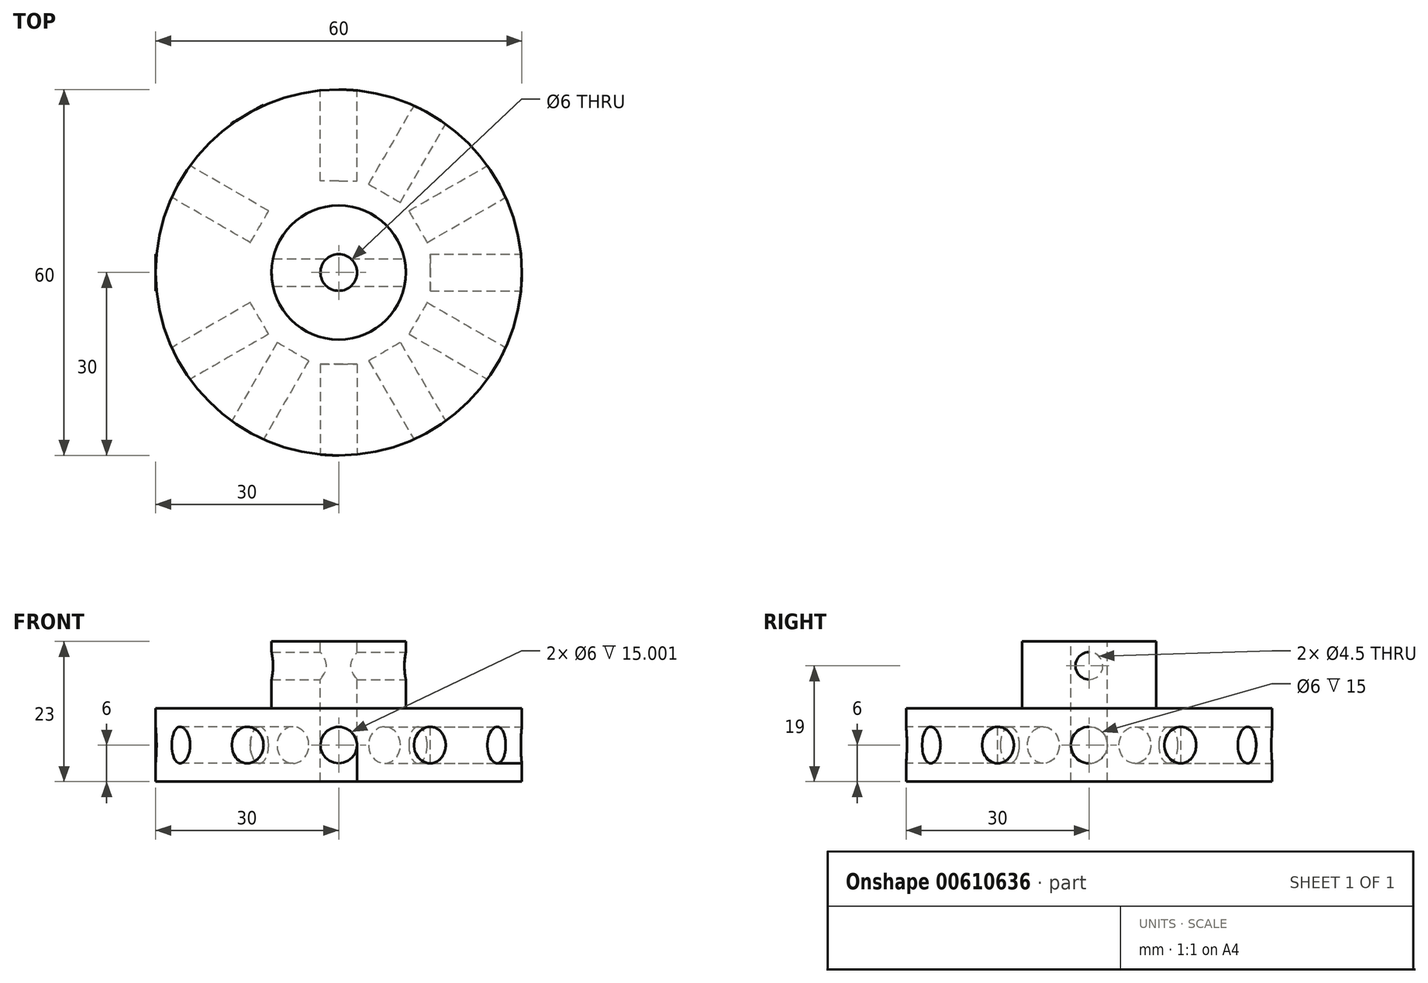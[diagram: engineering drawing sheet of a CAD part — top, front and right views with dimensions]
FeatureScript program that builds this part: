
annotation { "Feature Type Name" : "Feature", "Feature Type Description" : "" }
export const myFeature = defineFeature(function(context is Context, id is Id, definition is map)
    precondition{}
    {
        {
            assignVariable(context, id + "F0", {"name" : "Diam", "anyValue" : 60});
        }
        {
            assignVariable(context, id + "F1", {"name" : "Shaft_Dia", "anyValue" : 6});
        }
        {
            assignVariable(context, id + "F2", {"name" : "Hole_Depth", "anyValue" : 15});
        }
        {
            assignVariable(context, id + "F3", {"name" : "Hub_Thickness", "anyValue" : 12});
        }
        {
            var Q0;
            Q0=qCreatedBy(makeId("Top.planeOp"),FACE);
            var sketch = newSketch(context, id + "F4", { "sketchPlane" : qUnion([Q0])});
            skCircle(sketch, "E0", {"center": v(0, 0) * mm, "radius": 30 * mm});
            skSolve(sketch);
        }
        {
            var Q0;
            Q0=makeQuery(id+"F4.imprint","IMPRINT",FACE,{"disambiguationData":[TD([[makeQuery(id+"F4.imprint","IMPRINT",EDGE,{"derivedFrom":sQuery(id+"F4.wireOp",EDGE,"E0")}),1.0]])]});
            extrude(context, id + "F5", {"entities" : qUnion([Q0]), "depth" : (getVariable(context, 'Hub_Thickness')) * mm, "offsetDistance" : 25 * mm});
        }
        {
            var Q0;
            Q0=makeQuery(id+"F5.opExtrude","CAP_FACE",FACE,{"disambiguationData":[OSD([sQuery(id+"F4.wireOp",EDGE,"E0")])],"isStart":false});
            var sketch = newSketch(context, id + "F6", { "sketchPlane" : qUnion([Q0])});
            skCircle(sketch, "E1", {"center": v(0, 0) * mm, "radius": 11 * mm});
            skSolve(sketch);
        }
        {
            var Q0;
            Q0=makeQuery(id+"F6.imprint","IMPRINT",FACE,{"disambiguationData":[TD([[makeQuery(id+"F6.imprint","IMPRINT",EDGE,{"derivedFrom":sQuery(id+"F6.wireOp",EDGE,"E1")}),1.0]])]});
            extrude(context, id + "F7", {"entities" : qUnion([Q0]), "operationType" : NewBodyOperationType.ADD, "depth" : 11 * mm, "offsetDistance" : 25 * mm});
        }
        {
            var Q0;
            Q0=makeQuery(id+"F7.opExtrude","CAP_FACE",FACE,{"disambiguationData":[OSD([sQuery(id+"F6.wireOp",EDGE,"E1")])],"isStart":false});
            var sketch = newSketch(context, id + "F8", { "sketchPlane" : qUnion([Q0])});
            skPoint(sketch, "E2", {"position": v(0, 0) * mm});
            skSolve(sketch);
        }
        {
            var Q0;
            Q0=sQuery(id+"F8.wireOp",VERTEX,"E2");
            var Q1;
            Q1=makeQuery(id+"F5.opExtrude","SWEPT_BODY",BODY,{"disambiguationData":[OSD([sQuery(id+"F4.wireOp",EDGE,"E0")])]});
            hole(context, id + "F9", {"style" : HoleStyle.SIMPLE, "endStyle" : HoleEndStyle.THROUGH, "holeDiameter" : (getVariable(context, 'Shaft_Dia')) * mm, "majorDiameter" : 5 * mm, "tappedDepth" : 12 * mm, "tapClearance" : 3, "locations" : qUnion([Q0]), "scope" : qUnion([Q1])});
        }
        {
            var Q0;
            Q0=qCreatedBy(makeId("Right.planeOp"),FACE);
            var sketch = newSketch(context, id + "F10", { "sketchPlane" : qUnion([Q0])});
            skCircle(sketch, "E3", {"center": v(0, 19) * mm, "radius": 2.25 * mm});
            skSolve(sketch);
        }
        {
            var Q0;
            Q0 = qSketchRegion(id + "F10", true);
            extrude(context, id + "F11", {"entities" : qUnion([Q0]), "operationType" : NewBodyOperationType.REMOVE, "endBound" : BoundingType.SYMMETRIC, "oppositeDirection" : true, "depth" : 100 * mm, "offsetDistance" : 25 * mm});
        }
        {
            var Q0;
            Q0=qCreatedBy(makeId("Top.planeOp"),FACE);
            var sketch = newSketch(context, id + "F12", { "sketchPlane" : qUnion([Q0])});
            skPoint(sketch, "E4", {"position": v(-30, 0) * mm});
            skPoint(sketch, "E5.1.0", {"position": v(-25.98, -15) * mm});
            skPoint(sketch, "E5.2.0", {"position": v(-15, -25.98) * mm});
            skPoint(sketch, "E5.3.0", {"position": v(0, -30) * mm});
            skPoint(sketch, "E5.4.0", {"position": v(15, -25.98) * mm});
            skPoint(sketch, "E5.5.0", {"position": v(25.98, -15) * mm});
            skPoint(sketch, "E5.6.0", {"position": v(30, 0) * mm});
            skPoint(sketch, "E5.7.0", {"position": v(25.98, 15) * mm});
            skPoint(sketch, "E5.8.0", {"position": v(15, 25.98) * mm});
            skPoint(sketch, "E5.9.0", {"position": v(0, 30) * mm});
            skPoint(sketch, "E5.10.0", {"position": v(-15, 25.98) * mm});
            skPoint(sketch, "E5.11.0", {"position": v(-25.98, 15) * mm});
            skPoint(sketch, "E5.center", {"position": v(0, 0) * mm});
            skSolve(sketch);
        }
        {
            var Q0;
            Q0=qCreatedBy(makeId("Front.planeOp"),FACE);
            cPlane(context, id + "F13", {"entities" : qUnion([Q0]), "cplaneType" : CPlaneType.OFFSET, "offset" : (getVariable(context, 'Diam') / 2) * mm, "width" : 150 * mm, "height" : 150 * mm});
        }
        {
            var Q0;
            Q0=qCreatedBy(id+"F13.planeOp",FACE);
            var sketch = newSketch(context, id + "F14", { "sketchPlane" : qUnion([Q0])});
            skCircle(sketch, "E6", {"center": v(0, 6) * mm, "radius": 3 * mm});
            skSolve(sketch);
        }
        {
            var Q0;
            Q0=makeQuery(id+"F14.imprint","IMPRINT",FACE,{"disambiguationData":[TD([[makeQuery(id+"F14.imprint","IMPRINT",EDGE,{"derivedFrom":sQuery(id+"F14.wireOp",EDGE,"E6")}),1.0]])]});
            var Q1;
            Q1=sQuery(id+"F14.wireOp",EDGE,"E6");
            extrude(context, id + "F15", {"entities" : qUnion([Q0]), "operationType" : NewBodyOperationType.REMOVE, "surfaceEntities" : qUnion([Q1]), "oppositeDirection" : true, "depth" : (getVariable(context, 'Hole_Depth')) * mm, "offsetDistance" : 25 * mm});
        }
        {
            var Q0;
            Q0=qCreatedBy(makeId("Front.planeOp"),FACE);
            cPlane(context, id + "F16", {"entities" : qUnion([Q0]), "cplaneType" : CPlaneType.OFFSET, "offset" : (getVariable(context, 'Diam') / 2) * mm, "oppositeDirection" : true, "width" : 150 * mm, "height" : 150 * mm});
        }
        {
            var Q0;
            Q0=qCreatedBy(id+"F16.planeOp",FACE);
            var sketch = newSketch(context, id + "F17", { "sketchPlane" : qUnion([Q0])});
            skCircle(sketch, "E7", {"center": v(0, 6) * mm, "radius": 3 * mm});
            skSolve(sketch);
        }
        {
            var Q0;
            Q0=makeQuery(id+"F17.imprint","IMPRINT",FACE,{"disambiguationData":[TD([[makeQuery(id+"F17.imprint","IMPRINT",EDGE,{"derivedFrom":sQuery(id+"F17.wireOp",EDGE,"E7")}),1.0]])]});
            var Q1;
            Q1=sQuery(id+"F17.wireOp",EDGE,"E7");
            extrude(context, id + "F18", {"entities" : qUnion([Q0]), "operationType" : NewBodyOperationType.REMOVE, "surfaceEntities" : qUnion([Q1]), "depth" : (getVariable(context, 'Hole_Depth')) * mm, "offsetDistance" : 25 * mm});
        }
        {
            var Q0;
            Q0=qCreatedBy(makeId("Right.planeOp"),FACE);
            cPlane(context, id + "F19", {"entities" : qUnion([Q0]), "cplaneType" : CPlaneType.OFFSET, "offset" : (getVariable(context, 'Diam') / 2) * mm, "width" : 150 * mm, "height" : 150 * mm});
        }
        {
            var Q0;
            Q0=qCreatedBy(id+"F19.planeOp",FACE);
            var sketch = newSketch(context, id + "F20", { "sketchPlane" : qUnion([Q0])});
            skCircle(sketch, "E8", {"center": v(0, 6) * mm, "radius": 3 * mm});
            skSolve(sketch);
        }
        {
            var Q0;
            Q0=makeQuery(id+"F20.imprint","IMPRINT",FACE,{"disambiguationData":[TD([[makeQuery(id+"F20.imprint","IMPRINT",EDGE,{"derivedFrom":sQuery(id+"F20.wireOp",EDGE,"E8")}),1.0]])]});
            extrude(context, id + "F21", {"entities" : qUnion([Q0]), "operationType" : NewBodyOperationType.REMOVE, "oppositeDirection" : true, "depth" : (getVariable(context, 'Hole_Depth')) * mm, "offsetDistance" : 25 * mm});
        }
        {
            var Q0;
            Q0=qCreatedBy(makeId("Right.planeOp"),FACE);
            cPlane(context, id + "F22", {"entities" : qUnion([Q0]), "cplaneType" : CPlaneType.OFFSET, "offset" : (getVariable(context, 'Diam') / 2) * mm, "oppositeDirection" : true, "width" : 150 * mm, "height" : 150 * mm});
        }
        {
            var Q0;
            Q0=qCreatedBy(id+"F22.planeOp",FACE);
            var sketch = newSketch(context, id + "F23", { "sketchPlane" : qUnion([Q0])});
            skCircle(sketch, "E9", {"center": v(0, 6) * mm, "radius": 3 * mm});
            skSolve(sketch);
        }
        {
            var Q0;
            Q0=makeQuery(id+"F23.imprint","IMPRINT",FACE,{"disambiguationData":[TD([[makeQuery(id+"F23.imprint","IMPRINT",EDGE,{"derivedFrom":sQuery(id+"F23.wireOp",EDGE,"E9")}),1.0]])]});
            var Q1;
            Q1=sQuery(id+"F23.wireOp",EDGE,"E9");
            extrude(context, id + "F24", {"entities" : qUnion([Q0]), "operationType" : NewBodyOperationType.ADD, "surfaceEntities" : qUnion([Q1]), "depth" : (getVariable(context, 'Hole_Depth')) * mm, "offsetDistance" : 25 * mm});
        }
        {
            var Q0;
            Q0=sQuery(id+"F12.wireOp",VERTEX,"E5.11.0");
            var Q1;
            Q1=makeQuery(id+"F5.opExtrude","CAP_EDGE",EDGE,{"disambiguationData":[OSD([sQuery(id+"F4.wireOp",EDGE,"E0")])],"isStart":false});
            cPlane(context, id + "F25", {"entities" : qUnion([Q0, Q1]), "cplaneType" : CPlaneType.CURVE_POINT, "offset" : 25 * mm, "width" : 150 * mm, "height" : 150 * mm});
        }
        {
            var Q0;
            Q0=sQuery(id+"F12.wireOp",VERTEX,"E5.10.0");
            var Q1;
            Q1=makeQuery(id+"F5.opExtrude","CAP_EDGE",EDGE,{"disambiguationData":[OSD([sQuery(id+"F4.wireOp",EDGE,"E0")])],"isStart":false});
            cPlane(context, id + "F26", {"entities" : qUnion([Q0, Q1]), "cplaneType" : CPlaneType.CURVE_POINT, "offset" : 25 * mm, "width" : 150 * mm, "height" : 150 * mm});
        }
        {
            var Q0;
            Q0=sQuery(id+"F12.wireOp",VERTEX,"E5.8.0");
            var Q1;
            Q1=makeQuery(id+"F5.opExtrude","CAP_EDGE",EDGE,{"disambiguationData":[OSD([sQuery(id+"F4.wireOp",EDGE,"E0")])],"isStart":false});
            cPlane(context, id + "F27", {"entities" : qUnion([Q0, Q1]), "cplaneType" : CPlaneType.CURVE_POINT, "offset" : 25 * mm, "width" : 150 * mm, "height" : 150 * mm});
        }
        {
            var Q0;
            Q0=sQuery(id+"F12.wireOp",VERTEX,"E5.7.0");
            var Q1;
            Q1=makeQuery(id+"F5.opExtrude","CAP_EDGE",EDGE,{"disambiguationData":[OSD([sQuery(id+"F4.wireOp",EDGE,"E0")])],"isStart":false});
            cPlane(context, id + "F28", {"entities" : qUnion([Q0, Q1]), "cplaneType" : CPlaneType.CURVE_POINT, "offset" : 25 * mm, "width" : 150 * mm, "height" : 150 * mm});
        }
        {
            var Q0;
            Q0=qCreatedBy(id+"F25.planeOp",FACE);
            cPlane(context, id + "F29", {"entities" : qUnion([Q0]), "cplaneType" : CPlaneType.OFFSET, "offset" : (getVariable(context, 'Diam') / 2) * mm, "width" : 150 * mm, "height" : 150 * mm});
        }
        {
            var Q0;
            Q0=qCreatedBy(id+"F29.planeOp",FACE);
            var sketch = newSketch(context, id + "F30", { "sketchPlane" : qUnion([Q0])});
            skCircle(sketch, "E10", {"center": v(0, 6) * mm, "radius": 3 * mm});
            skSolve(sketch);
        }
        {
            var Q0;
            Q0=makeQuery(id+"F30.imprint","IMPRINT",FACE,{"disambiguationData":[TD([[makeQuery(id+"F30.imprint","IMPRINT",EDGE,{"derivedFrom":sQuery(id+"F30.wireOp",EDGE,"E10")}),1.0]])]});
            extrude(context, id + "F31", {"entities" : qUnion([Q0]), "operationType" : NewBodyOperationType.REMOVE, "oppositeDirection" : true, "depth" : 15 * mm, "offsetDistance" : 25 * mm});
        }
        {
            var Q0;
            Q0=qCreatedBy(id+"F25.planeOp",FACE);
            cPlane(context, id + "F32", {"entities" : qUnion([Q0]), "cplaneType" : CPlaneType.OFFSET, "offset" : (getVariable(context, 'Diam') / 2) * mm, "oppositeDirection" : true, "width" : 150 * mm, "height" : 150 * mm});
        }
        {
            var Q0;
            Q0=qCreatedBy(id+"F32.planeOp",FACE);
            var sketch = newSketch(context, id + "F33", { "sketchPlane" : qUnion([Q0])});
            skCircle(sketch, "E11", {"center": v(0, 6) * mm, "radius": 3 * mm});
            skSolve(sketch);
        }
        {
            var Q0;
            Q0 = qSketchRegion(id + "F33", true);
            extrude(context, id + "F34", {"entities" : qUnion([Q0]), "operationType" : NewBodyOperationType.REMOVE, "depth" : (getVariable(context, 'Hole_Depth')) * mm, "offsetDistance" : 25 * mm});
        }
        {
            var Q0;
            Q0=qCreatedBy(id+"F26.planeOp",FACE);
            cPlane(context, id + "F35", {"entities" : qUnion([Q0]), "cplaneType" : CPlaneType.OFFSET, "offset" : (getVariable(context, 'Diam') / 2) * mm, "oppositeDirection" : true, "width" : 150 * mm, "height" : 150 * mm});
        }
        {
            var Q0;
            Q0=qCreatedBy(id+"F35.planeOp",FACE);
            var sketch = newSketch(context, id + "F36", { "sketchPlane" : qUnion([Q0])});
            skCircle(sketch, "E12", {"center": v(0, 6) * mm, "radius": 3 * mm});
            skSolve(sketch);
        }
        {
            var Q0;
            Q0 = qSketchRegion(id + "F36", true);
            extrude(context, id + "F37", {"entities" : qUnion([Q0]), "operationType" : NewBodyOperationType.REMOVE, "depth" : (getVariable(context, 'Hole_Depth')) * mm, "offsetDistance" : 25 * mm});
        }
        {
            var Q0;
            Q0=qCreatedBy(id+"F27.planeOp",FACE);
            cPlane(context, id + "F38", {"entities" : qUnion([Q0]), "cplaneType" : CPlaneType.OFFSET, "offset" : (getVariable(context, 'Diam') / 2) * mm, "oppositeDirection" : true, "width" : 150 * mm, "height" : 150 * mm});
        }
        {
            var Q0;
            Q0=qCreatedBy(id+"F38.planeOp",FACE);
            var sketch = newSketch(context, id + "F39", { "sketchPlane" : qUnion([Q0])});
            skCircle(sketch, "E13", {"center": v(0, 6) * mm, "radius": 3 * mm});
            skSolve(sketch);
        }
        {
            var Q0;
            Q0 = qSketchRegion(id + "F39", true);
            extrude(context, id + "F40", {"entities" : qUnion([Q0]), "operationType" : NewBodyOperationType.REMOVE, "depth" : (getVariable(context, 'Hole_Depth')) * mm, "offsetDistance" : 25 * mm});
        }
        {
            var Q0;
            Q0=qCreatedBy(id+"F28.planeOp",FACE);
            cPlane(context, id + "F41", {"entities" : qUnion([Q0]), "cplaneType" : CPlaneType.OFFSET, "offset" : (getVariable(context, 'Diam') / 2) * mm, "oppositeDirection" : true, "width" : 150 * mm, "height" : 150 * mm});
        }
        {
            var Q0;
            Q0=qCreatedBy(id+"F41.planeOp",FACE);
            var sketch = newSketch(context, id + "F42", { "sketchPlane" : qUnion([Q0])});
            skCircle(sketch, "E14", {"center": v(0, 6) * mm, "radius": 3 * mm});
            skSolve(sketch);
        }
        {
            var Q0;
            Q0 = qSketchRegion(id + "F42", true);
            extrude(context, id + "F43", {"entities" : qUnion([Q0]), "operationType" : NewBodyOperationType.REMOVE, "depth" : (getVariable(context, 'Hole_Depth')) * mm, "offsetDistance" : 25 * mm});
        }
        {
            var Q0;
            Q0=qCreatedBy(id+"F26.planeOp",FACE);
            cPlane(context, id + "F44", {"entities" : qUnion([Q0]), "cplaneType" : CPlaneType.OFFSET, "offset" : (getVariable(context, 'Diam') / 2) * mm, "width" : 150 * mm, "height" : 150 * mm});
        }
        {
            var Q0;
            Q0=qCreatedBy(id+"F44.planeOp",FACE);
            var sketch = newSketch(context, id + "F45", { "sketchPlane" : qUnion([Q0])});
            skCircle(sketch, "E15", {"center": v(0, 6) * mm, "radius": 3 * mm});
            skSolve(sketch);
        }
        {
            var Q0;
            Q0 = qSketchRegion(id + "F45", true);
            extrude(context, id + "F46", {"entities" : qUnion([Q0]), "operationType" : NewBodyOperationType.REMOVE, "oppositeDirection" : true, "depth" : (getVariable(context, 'Hole_Depth')) * mm, "offsetDistance" : 25 * mm});
        }
        {
            var Q0;
            Q0=qCreatedBy(id+"F27.planeOp",FACE);
            cPlane(context, id + "F47", {"entities" : qUnion([Q0]), "cplaneType" : CPlaneType.OFFSET, "offset" : (getVariable(context, 'Diam') / 2) * mm, "width" : 150 * mm, "height" : 150 * mm});
        }
        {
            var Q0;
            Q0=qCreatedBy(id+"F47.planeOp",FACE);
            var sketch = newSketch(context, id + "F48", { "sketchPlane" : qUnion([Q0])});
            skCircle(sketch, "E16", {"center": v(0, 6) * mm, "radius": 3 * mm});
            skSolve(sketch);
        }
        {
            var Q0;
            Q0 = qSketchRegion(id + "F48", true);
            extrude(context, id + "F49", {"entities" : qUnion([Q0]), "operationType" : NewBodyOperationType.REMOVE, "oppositeDirection" : true, "depth" : (getVariable(context, 'Hole_Depth')) * mm, "offsetDistance" : 25 * mm});
        }
        {
            var Q0;
            Q0=qCreatedBy(id+"F28.planeOp",FACE);
            cPlane(context, id + "F50", {"entities" : qUnion([Q0]), "cplaneType" : CPlaneType.OFFSET, "offset" : (getVariable(context, 'Diam') / 2) * mm, "width" : 150 * mm, "height" : 150 * mm});
        }
        {
            var Q0;
            Q0=qCreatedBy(id+"F50.planeOp",FACE);
            var sketch = newSketch(context, id + "F51", { "sketchPlane" : qUnion([Q0])});
            skCircle(sketch, "E17", {"center": v(0, 6) * mm, "radius": 3 * mm});
            skSolve(sketch);
        }
        {
            var Q0;
            Q0 = qSketchRegion(id + "F51", true);
            extrude(context, id + "F52", {"entities" : qUnion([Q0]), "operationType" : NewBodyOperationType.ADD, "oppositeDirection" : true, "depth" : (getVariable(context, 'Hole_Depth')) * mm, "offsetDistance" : 25 * mm});
        }
    });
